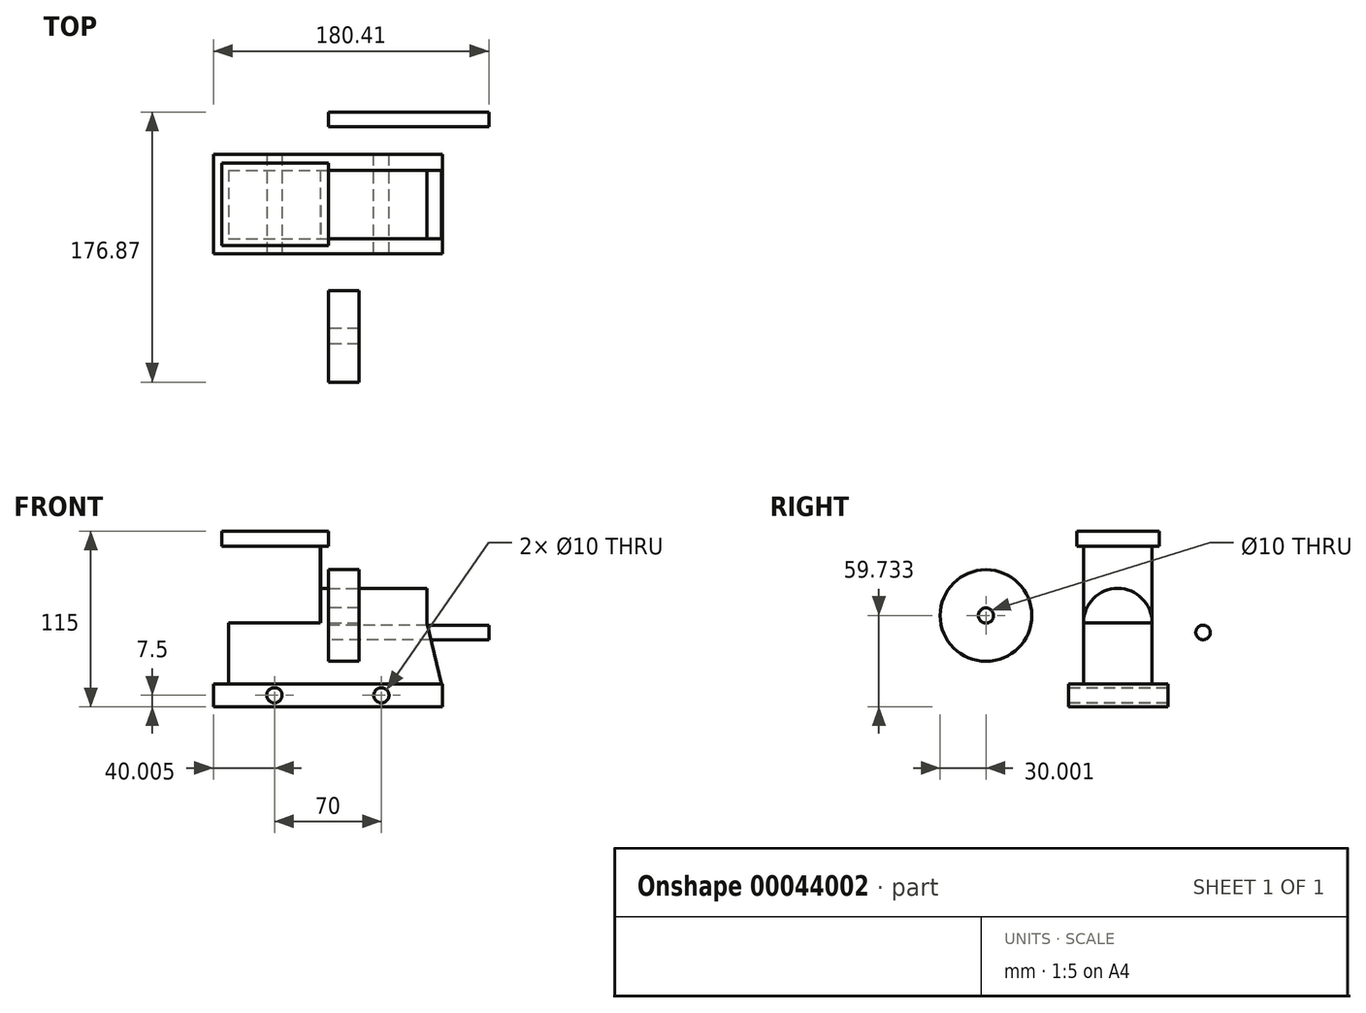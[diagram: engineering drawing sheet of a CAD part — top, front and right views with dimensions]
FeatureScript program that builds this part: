
annotation { "Feature Type Name" : "Feature", "Feature Type Description" : "" }
export const myFeature = defineFeature(function(context is Context, id is Id, definition is map)
    precondition{}
    {
        {
            var Q0;
            Q0=qCreatedBy(makeId("Top.planeOp"),FACE);
            var sketch = newSketch(context, id + "F0", { "sketchPlane" : qUnion([Q0])});
            skLineSegment(sketch, "E0.bottom", {"start": v(-75.4, 27.35) * mm, "end": v(74.6, 27.35) * mm});
            skLineSegment(sketch, "E0.top", {"start": v(-75.4, -37.65) * mm, "end": v(74.6, -37.65) * mm});
            skLineSegment(sketch, "E0.left", {"start": v(-75.4, 27.35) * mm, "end": v(-75.4, -37.65) * mm});
            skLineSegment(sketch, "E0.right", {"start": v(74.6, 27.35) * mm, "end": v(74.6, -37.65) * mm});
            skSolve(sketch);
        }
        {
            var Q0;
            Q0=makeQuery(id+"F0.imprint","IMPRINT",FACE,{"disambiguationData":[TD([[makeQuery(id+"F0.imprint","IMPRINT",EDGE,{"derivedFrom":sQuery(id+"F0.wireOp",EDGE,"E0.bottom")}),-1.0]])]});
            extrude(context, id + "F1", {"entities" : qUnion([Q0]), "depth" : 15 * mm});
        }
        {
            var Q0;
            Q0=makeQuery(id+"F1.opExtrude","CAP_FACE",FACE,{"disambiguationData":[OSD([sQuery(id+"F0.wireOp",EDGE,"E0.bottom"),sQuery(id+"F0.wireOp",EDGE,"E0.top"),sQuery(id+"F0.wireOp",EDGE,"E0.left"),sQuery(id+"F0.wireOp",EDGE,"E0.right")])],"isStart":false});
            var sketch = newSketch(context, id + "F2", { "sketchPlane" : qUnion([Q0])});
            skLineSegment(sketch, "E1", {"start": v(-75.4, 17.35) * mm, "end": v(-65.4, 17.35) * mm});
            skLineSegment(sketch, "E2", {"start": v(-65.4, 17.35) * mm, "end": v(-65.4, 27.35) * mm});
            skLineSegment(sketch, "E3", {"start": v(-75.4, -27.65) * mm, "end": v(-65.4, -27.65) * mm});
            skLineSegment(sketch, "E4", {"start": v(-65.4, -27.65) * mm, "end": v(-65.4, -37.65) * mm});
            skLineSegment(sketch, "E5", {"start": v(74.6, 17.35) * mm, "end": v(64.6, 17.35) * mm});
            skLineSegment(sketch, "E6", {"start": v(64.6, 17.35) * mm, "end": v(64.6, 27.35) * mm});
            skLineSegment(sketch, "E7", {"start": v(74.6, -27.65) * mm, "end": v(64.6, -27.65) * mm});
            skLineSegment(sketch, "E8", {"start": v(64.6, -27.65) * mm, "end": v(64.6, -37.65) * mm});
            skSolve(sketch);
        }
        {
            var Q0;
            {var subQ2=sQuery(id+"F2.wireOp",EDGE,"E1");Q0=makeQuery(id+"F2.imprint","IMPRINT",FACE,{"disambiguationData":[TD([[makeQuery(id+"F2.imprint","IMPRINT",EDGE,{"derivedFrom":subQ2}),-1.0]])]});}
            var sketch = newSketch(context, id + "F3", { "sketchPlane" : qUnion([Q0])});
            skLineSegment(sketch, "E9.bottom", {"start": v(-65.48, 16.92) * mm, "end": v(64.52, 16.92) * mm});
            skLineSegment(sketch, "E9.top", {"start": v(-65.48, -28.08) * mm, "end": v(64.52, -28.08) * mm});
            skLineSegment(sketch, "E9.left", {"start": v(-65.48, 16.92) * mm, "end": v(-65.48, -28.08) * mm});
            skLineSegment(sketch, "E9.right", {"start": v(64.52, 16.92) * mm, "end": v(64.52, -28.08) * mm});
            skSolve(sketch);
        }
        {
            var Q0;
            {var subQ8=sQuery(id+"F3.wireOp",EDGE,"E9.bottom");Q0=makeQuery(id+"F3.imprint","IMPRINT",FACE,{"disambiguationData":[TD([[makeQuery(id+"F3.imprint","IMPRINT",EDGE,{"derivedFrom":subQ8}),-1.0]])]});}
            extrude(context, id + "F4", {"entities" : qUnion([Q0]), "operationType" : NewBodyOperationType.ADD, "depth" : 40 * mm});
        }
        {
            var Q0;
            Q0=makeQuery(id+"F4.opExtrude","SWEPT_FACE",FACE,{"disambiguationData":[OSD([sQuery(id+"F3.wireOp",EDGE,"E9.right")])]});
            var sketch = newSketch(context, id + "F5", { "sketchPlane" : qUnion([Q0])});
            skArc(sketch, "E10", {"start": v(16.92, 55) * mm, "mid": v(-5.58, 77.5) * mm, "end": v(-28.08, 55) * mm});
            skSolve(sketch);
        }
        {
            var Q0;
            Q0=makeQuery(id+"F5.imprint","IMPRINT",FACE,{"disambiguationData":[TD([[makeQuery(id+"F5.imprint","IMPRINT",EDGE,{"derivedFrom":sQuery(id+"F5.wireOp",EDGE,"E10")}),1.0]])]});
            extrude(context, id + "F6", {"entities" : qUnion([Q0]), "oppositeDirection" : true, "depth" : 70 * mm});
        }
        {
            var Q0;
            Q0=makeQuery(id+"F4.opExtrude","SWEPT_FACE",FACE,{"disambiguationData":[OSD([sQuery(id+"F3.wireOp",EDGE,"E9.bottom")])]});
            var sketch = newSketch(context, id + "F7", { "sketchPlane" : qUnion([Q0])});
            skLineSegment(sketch, "E11", {"start": v(-64.52, 55) * mm, "end": v(-74, 14.8) * mm});
            skLineSegment(sketch, "E12", {"start": v(-64.52, 15) * mm, "end": v(-74, 14.8) * mm});
            skLineSegment(sketch, "E13", {"start": v(-64.52, 55) * mm, "end": v(-64.52, 15) * mm});
            skSolve(sketch);
        }
        {
            var Q0;
            Q0=makeQuery(id+"F7.imprint","IMPRINT",FACE,{"disambiguationData":[TD([[makeQuery(id+"F7.imprint","IMPRINT",EDGE,{"derivedFrom":sQuery(id+"F7.wireOp",EDGE,"E11")}),1.0]])]});
            extrude(context, id + "F8", {"entities" : qUnion([Q0]), "operationType" : NewBodyOperationType.ADD, "oppositeDirection" : true, "depth" : 45 * mm});
        }
        {
            var Q0;
            Q0=makeQuery(id+"F4.opExtrude","CAP_FACE",FACE,{"disambiguationData":[OSD([sQuery(id+"F2.wireOp",EDGE,"E3"),sQuery(id+"F2.wireOp",EDGE,"E4"),sQuery(id+"F3.wireOp",EDGE,"E9.bottom"),sQuery(id+"F3.wireOp",EDGE,"E9.top"),sQuery(id+"F3.wireOp",EDGE,"E9.left"),sQuery(id+"F3.wireOp",EDGE,"E9.right")])],"isStart":false});
            var sketch = newSketch(context, id + "F9", { "sketchPlane" : qUnion([Q0])});
            skLineSegment(sketch, "E14", {"start": v(-4.98, -28.08) * mm, "end": v(-65.4, -27.65) * mm});
            skLineSegment(sketch, "E15", {"start": v(-65.4, -27.65) * mm, "end": v(-65.48, 16.92) * mm});
            skLineSegment(sketch, "E16", {"start": v(-65.48, 16.92) * mm, "end": v(-5.48, 16.92) * mm});
            skLineSegment(sketch, "E17", {"start": v(-5.48, 16.92) * mm, "end": v(-4.98, -28.08) * mm});
            skSolve(sketch);
        }
        {
            var Q0;
            Q0=makeQuery(id+"F9.imprint","IMPRINT",FACE,{"disambiguationData":[TD([[makeQuery(id+"F9.imprint","IMPRINT",EDGE,{"derivedFrom":sQuery(id+"F9.wireOp",EDGE,"E14")}),-1.0]])]});
            extrude(context, id + "F10", {"entities" : qUnion([Q0]), "depth" : 50 * mm});
        }
        {
            var Q0;
            Q0=makeQuery(id+"F10.opExtrude","CAP_FACE",FACE,{"disambiguationData":[OSD([sQuery(id+"F9.wireOp",EDGE,"E14"),sQuery(id+"F9.wireOp",EDGE,"E15"),sQuery(id+"F9.wireOp",EDGE,"E16"),sQuery(id+"F9.wireOp",EDGE,"E17")])],"isStart":false});
            var sketch = newSketch(context, id + "F11", { "sketchPlane" : qUnion([Q0])});
            skLineSegment(sketch, "E18.bottom", {"start": v(-70, 21.7) * mm, "end": v(0, 21.7) * mm});
            skLineSegment(sketch, "E18.top", {"start": v(-70, -32.3) * mm, "end": v(0, -32.3) * mm});
            skLineSegment(sketch, "E18.left", {"start": v(-70, 21.7) * mm, "end": v(-70, -32.3) * mm});
            skLineSegment(sketch, "E18.right", {"start": v(0, 21.7) * mm, "end": v(0, -32.3) * mm});
            skSolve(sketch);
        }
        {
            var Q0;
            Q0 = qSketchRegion(id + "F11", true);
            extrude(context, id + "F12", {"entities" : qUnion([Q0]), "operationType" : NewBodyOperationType.ADD, "depth" : 10 * mm});
        }
        {
            var Q0;
            Q0=makeQuery(id+"F1.opExtrude","SWEPT_FACE",FACE,{"disambiguationData":[OSD([sQuery(id+"F0.wireOp",EDGE,"E0.bottom")])]});
            var sketch = newSketch(context, id + "F13", { "sketchPlane" : qUnion([Q0])});
            skLineSegment(sketch, "E19", {"start": v(-74.6, 7.5) * mm, "end": v(-34.6, 7.5) * mm, "construction": true});
            skCircle(sketch, "E20", {"center": v(-34.6, 7.5) * mm, "radius": 5 * mm});
            skSolve(sketch);
        }
        {
            var Q0;
            Q0=qCreatedBy(makeId("Right.planeOp"),FACE);
            var sketch = newSketch(context, id + "F14", { "sketchPlane" : qUnion([Q0])});
            skCircle(sketch, "E21", {"center": v(-77.59, 0) * mm, "radius": 30 * mm});
            skSolve(sketch);
        }
        {
            var Q0;
            Q0 = qSketchRegion(id + "F14", true);
            extrude(context, id + "F15", {"entities" : qUnion([Q0]), "depth" : 20 * mm});
        }
        {
            var Q0;
            Q0=makeQuery(id+"F15.opExtrude","CAP_FACE",FACE,{"disambiguationData":[OSD([sQuery(id+"F14.wireOp",EDGE,"E21")])],"isStart":true});
            var sketch = newSketch(context, id + "F16", { "sketchPlane" : qUnion([Q0])});
            skCircle(sketch, "E22", {"center": v(77.59, 0) * mm, "radius": 5 * mm});
            skSolve(sketch);
        }
        {
            var Q0;
            Q0=makeQuery(id+"F16.imprint","IMPRINT",FACE,{"disambiguationData":[TD([[makeQuery(id+"F16.imprint","IMPRINT",EDGE,{"derivedFrom":sQuery(id+"F16.wireOp",EDGE,"E22")}),1.0]])]});
            extrude(context, id + "F17", {"entities" : qUnion([Q0]), "operationType" : NewBodyOperationType.REMOVE, "oppositeDirection" : true, "depth" : 25 * mm});
        }
        {
            var Q0;
            Q0=makeQuery(id+"F1.opExtrude","SWEPT_FACE",FACE,{"disambiguationData":[OSD([sQuery(id+"F0.wireOp",EDGE,"E0.top")])]});
            var sketch = newSketch(context, id + "F18", { "sketchPlane" : qUnion([Q0])});
            skLineSegment(sketch, "E23", {"start": v(-75.4, 7.5) * mm, "end": v(-35.4, 7.5) * mm, "construction": true});
            skCircle(sketch, "E24", {"center": v(-35.4, 7.5) * mm, "radius": 5 * mm});
            skSolve(sketch);
        }
        {
            var Q0;
            Q0=makeQuery(id+"F18.imprint","IMPRINT",FACE,{"disambiguationData":[TD([[makeQuery(id+"F18.imprint","IMPRINT",EDGE,{"derivedFrom":sQuery(id+"F18.wireOp",EDGE,"E24")}),1.0]])]});
            extrude(context, id + "F19", {"entities" : qUnion([Q0]), "operationType" : NewBodyOperationType.REMOVE, "oppositeDirection" : true, "depth" : 500 * mm});
        }
        {
            var Q0;
            Q0=makeQuery(id+"F13.imprint","IMPRINT",FACE,{"disambiguationData":[TD([[makeQuery(id+"F13.imprint","IMPRINT",EDGE,{"derivedFrom":sQuery(id+"F13.wireOp",EDGE,"E20")}),1.0]])]});
            extrude(context, id + "F20", {"entities" : qUnion([Q0]), "operationType" : NewBodyOperationType.REMOVE, "oppositeDirection" : true, "depth" : 500 * mm});
        }
        {
            var Q0;
            Q0=makeQuery(id+"F15.opExtrude","SWEPT_BODY",BODY,{"disambiguationData":[OSD([sQuery(id+"F14.wireOp",EDGE,"E21")])]});
            transform(context, id + "F21", {"entities" : qUnion([Q0]), "transformType" : TransformType.TRANSLATION_3D, "dx" : 0 * mm, "dy" : -14.26 * mm, "dz" : 59.73 * mm, "makeCopy" : false});
        }
        {
            var Q0;
            Q0=makeQuery(id+"F15.opExtrude","SWEPT_BODY",BODY,{"disambiguationData":[OSD([sQuery(id+"F14.wireOp",EDGE,"E21")])]});
            transform(context, id + "F22", {"entities" : qUnion([Q0]), "transformType" : TransformType.TRANSLATION_3D, "dx" : 33.48 * mm, "dy" : 7.8 * mm, "dz" : -22.6 * mm, "makeCopy" : true});
        }
        {
            var Q0;
            Q0=makeQuery(id+"F15.opExtrude","SWEPT_BODY",BODY,{"disambiguationData":[OSD([sQuery(id+"F14.wireOp",EDGE,"E21")])]});
            transform(context, id + "F23", {"entities" : qUnion([Q0]), "transformType" : TransformType.TRANSLATION_3D, "dx" : 0 * mm, "dy" : -14.18 * mm, "dz" : 151.67 * mm, "makeCopy" : true});
        }
        {
            var Q0;
            Q0=makeQuery(id+"F22.opPattern","COPY",BODY,{"derivedFrom":makeQuery(id+"F15.opExtrude","SWEPT_BODY",BODY,{"disambiguationData":[OSD([sQuery(id+"F14.wireOp",EDGE,"E21")])]}),"instanceName":"1"});
            var Q1;
            Q1=makeQuery(id+"F23.opPattern","COPY",BODY,{"derivedFrom":makeQuery(id+"F15.opExtrude","SWEPT_BODY",BODY,{"disambiguationData":[OSD([sQuery(id+"F14.wireOp",EDGE,"E21")])]}),"instanceName":"1"});
            deleteBodies(context, id + "F24", {"entities" : qUnion([Q0, Q1])});
        }
        {
            var Q0;
            Q0=qCreatedBy(makeId("Right.planeOp"),FACE);
            var sketch = newSketch(context, id + "F25", { "sketchPlane" : qUnion([Q0])});
            skCircle(sketch, "E25", {"center": v(50.27, 48.64) * mm, "radius": 4.75 * mm});
            skSolve(sketch);
        }
        {
            var Q0;
            Q0 = qSketchRegion(id + "F25", true);
            extrude(context, id + "F26", {"entities" : qUnion([Q0]), "depth" : 105 * mm});
        }
        {
            var Q0;
            Q0=makeQuery(id+"F10.opExtrude","SWEPT_FACE",FACE,{"disambiguationData":[OSD([sQuery(id+"F9.wireOp",EDGE,"E14")])]});
            var sketch = newSketch(context, id + "F27", { "sketchPlane" : qUnion([Q0])});
            skLineSegment(sketch, "E26", {"start": v(-4.78, 80) * mm, "end": v(-65.2, 80) * mm, "construction": true});
            skLineSegment(sketch, "E27", {"start": v(-35, 105) * mm, "end": v(-35, 55) * mm, "construction": true});
            skPoint(sketch, "E27.endSnap0", {"position": v(-35.25, 55) * mm});
            skCircle(sketch, "E28", {"center": v(-35, 80) * mm, "radius": 17.5 * mm});
            skSolve(sketch);
        }
        {
            var Q0;
            Q0=makeQuery(id+"F27.imprint","IMPRINT",FACE,{"disambiguationData":[TD([[makeQuery(id+"F27.imprint","IMPRINT",EDGE,{"derivedFrom":sQuery(id+"F27.wireOp",EDGE,"E28")}),1.0]])]});
            var sketch = newSketch(context, id + "F28", { "sketchPlane" : qUnion([Q0])});
            skSolve(sketch);
        }
        {
            var Q0;
            Q0 = qSketchRegion(id + "F28", true);
            var Q1;
            Q1=makeQuery(id+"F27.imprint","IMPRINT",FACE,{"disambiguationData":[TD([[makeQuery(id+"F27.imprint","IMPRINT",EDGE,{"derivedFrom":sQuery(id+"F27.wireOp",EDGE,"E28")}),1.0]])]});
            extrude(context, id + "F29", {"entities" : qUnion([Q0, Q1]), "operationType" : NewBodyOperationType.REMOVE, "oppositeDirection" : true, "depth" : 200 * mm});
        }
    });
